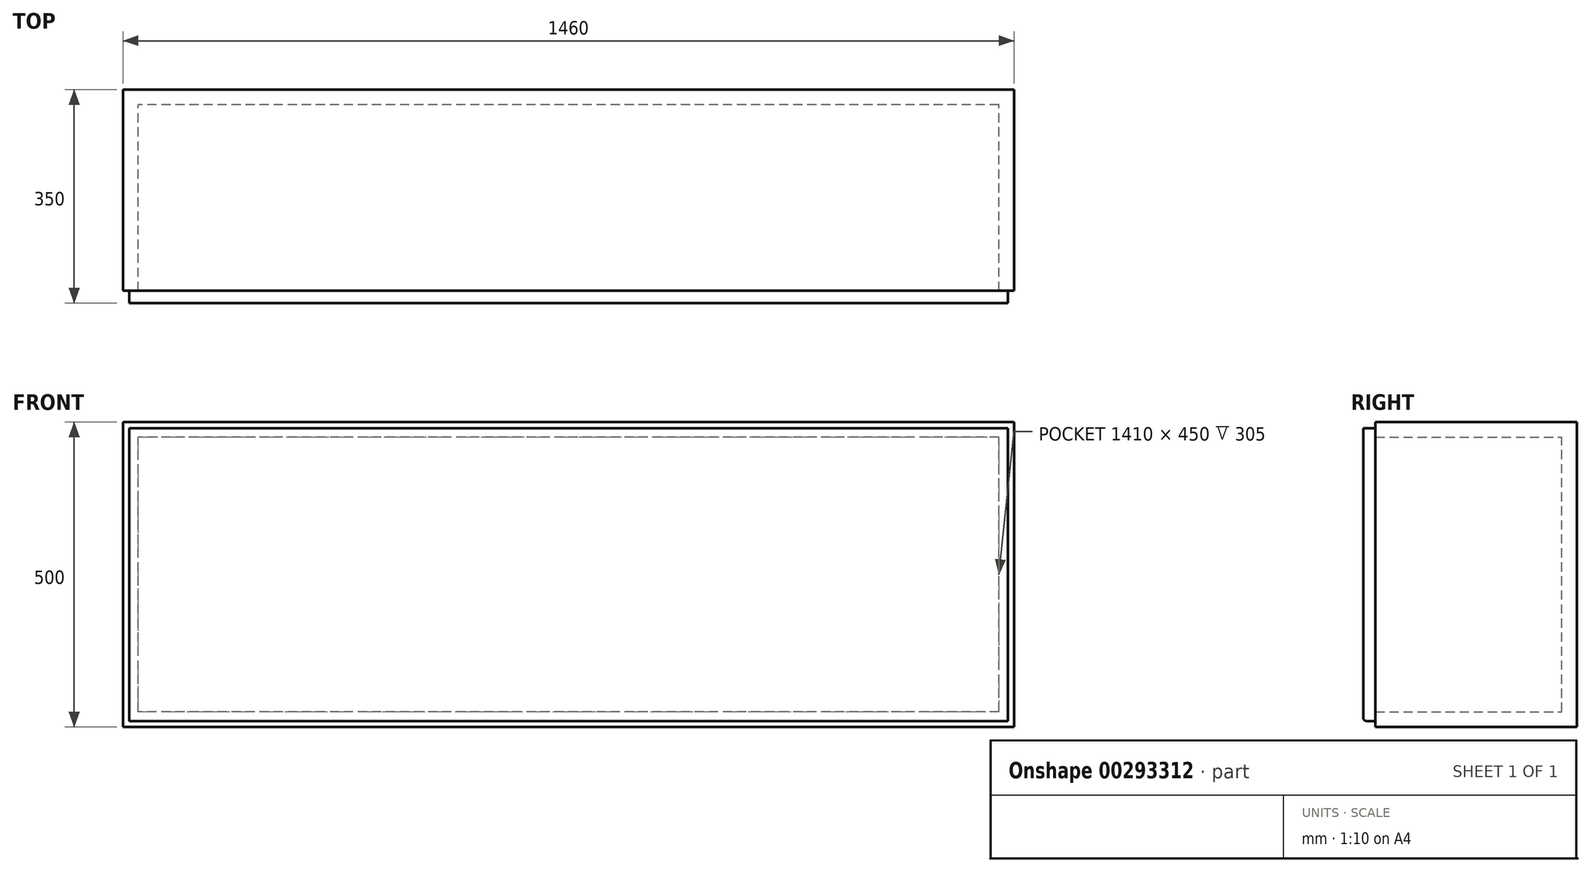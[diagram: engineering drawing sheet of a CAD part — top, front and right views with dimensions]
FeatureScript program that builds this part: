
annotation { "Feature Type Name" : "Feature", "Feature Type Description" : "" }
export const myFeature = defineFeature(function(context is Context, id is Id, definition is map)
    precondition{}
    {
        {
            var Q0;
            Q0=qCreatedBy(makeId("Front.planeOp"),FACE);
            var sketch = newSketch(context, id + "F0", { "sketchPlane" : qUnion([Q0])});
            skLineSegment(sketch, "E0.bottom", {"start": v(730, 0) * mm, "end": v(-730, 0) * mm});
            skLineSegment(sketch, "E0.top", {"start": v(730, 500) * mm, "end": v(-730, 500) * mm});
            skLineSegment(sketch, "E0.left", {"start": v(730, 0) * mm, "end": v(730, 500) * mm});
            skLineSegment(sketch, "E0.right", {"start": v(-730, 0) * mm, "end": v(-730, 500) * mm});
            skPoint(sketch, "E0.middle", {"position": v(0, 250) * mm});
            skSolve(sketch);
        }
        {
            var Q0;
            Q0=qSketchRegion(id+"F0",true);
            extrude(context, id + "F1", {"entities" : qUnion([Q0]), "depth" : 330 * mm});
        }
        {
            var Q0;
            Q0=makeQuery(id+"F1.opExtrude","CAP_FACE",FACE,{"disambiguationData":[OSD([sQuery(id+"F0.wireOp",EDGE,"E0.bottom"),sQuery(id+"F0.wireOp",EDGE,"E0.top"),sQuery(id+"F0.wireOp",EDGE,"E0.left"),sQuery(id+"F0.wireOp",EDGE,"E0.right")])],"isStart":false});
            shell(context, id + "F2", {"entities" : qUnion([Q0]), "thickness" : 25 * mm});
        }
        {
            var Q0;
            {var subQ0=sQuery(id+"F0.wireOp",EDGE,"E0.right");var subQ1=sQuery(id+"F0.wireOp",EDGE,"E0.left");var subQ2=sQuery(id+"F0.wireOp",EDGE,"E0.top");var subQ3=sQuery(id+"F0.wireOp",EDGE,"E0.bottom");Q0=makeQuery(id+"FIIPNUbMOw2rQ1R_1.boolean.opBoolean","MERGE",FACE,{"derivedFrom":[makeQuery(id+"F1.opExtrude","CAP_FACE",FACE,{"disambiguationData":[OSD([subQ3,subQ2,subQ1,subQ0])],"isStart":false}),makeQuery(id+"FIIPNUbMOw2rQ1R_1.opExtrude","CAP_FACE",FACE,{"disambiguationData":[OSD([subQ3,subQ2,subQ1,subQ0])],"isStart":false})]});}
            var sketch = newSketch(context, id + "F3", { "sketchPlane" : qUnion([Q0])});
            skLineSegment(sketch, "E1.bottom", {"start": v(-720, 490) * mm, "end": v(720, 490) * mm});
            skLineSegment(sketch, "E1.top", {"start": v(-720, 10) * mm, "end": v(720, 10) * mm});
            skLineSegment(sketch, "E1.left", {"start": v(-720, 490) * mm, "end": v(-720, 10) * mm});
            skLineSegment(sketch, "E1.right", {"start": v(720, 490) * mm, "end": v(720, 10) * mm});
            skSolve(sketch);
        }
        {
            var Q0;
            Q0=qSketchRegion(id+"F3",true);
            extrude(context, id + "F4", {"entities" : qUnion([Q0]), "depth" : 20 * mm});
        }
        {
            var Q0;
            Q0=makeQuery(id+"F4.opExtrude","CAP_EDGE",EDGE,{"disambiguationData":[OSD([sQuery(id+"F3.wireOp",EDGE,"E1.top")])],"isStart":false});
            var Q1;
            Q1=makeQuery(id+"F4.opExtrude","CAP_EDGE",EDGE,{"disambiguationData":[OSD([sQuery(id+"F3.wireOp",EDGE,"K9zKZkPS-6BRu-8GoP-H2SI-CPNL41GJwIiS.top")])],"isStart":false});
            fillet(context, id + "F5", {"entities" : qUnion([Q0, Q1]), "radius" : 5 * mm, "tangentPropagation" : true, "allowEdgeOverflow" : false});
        }
    });
